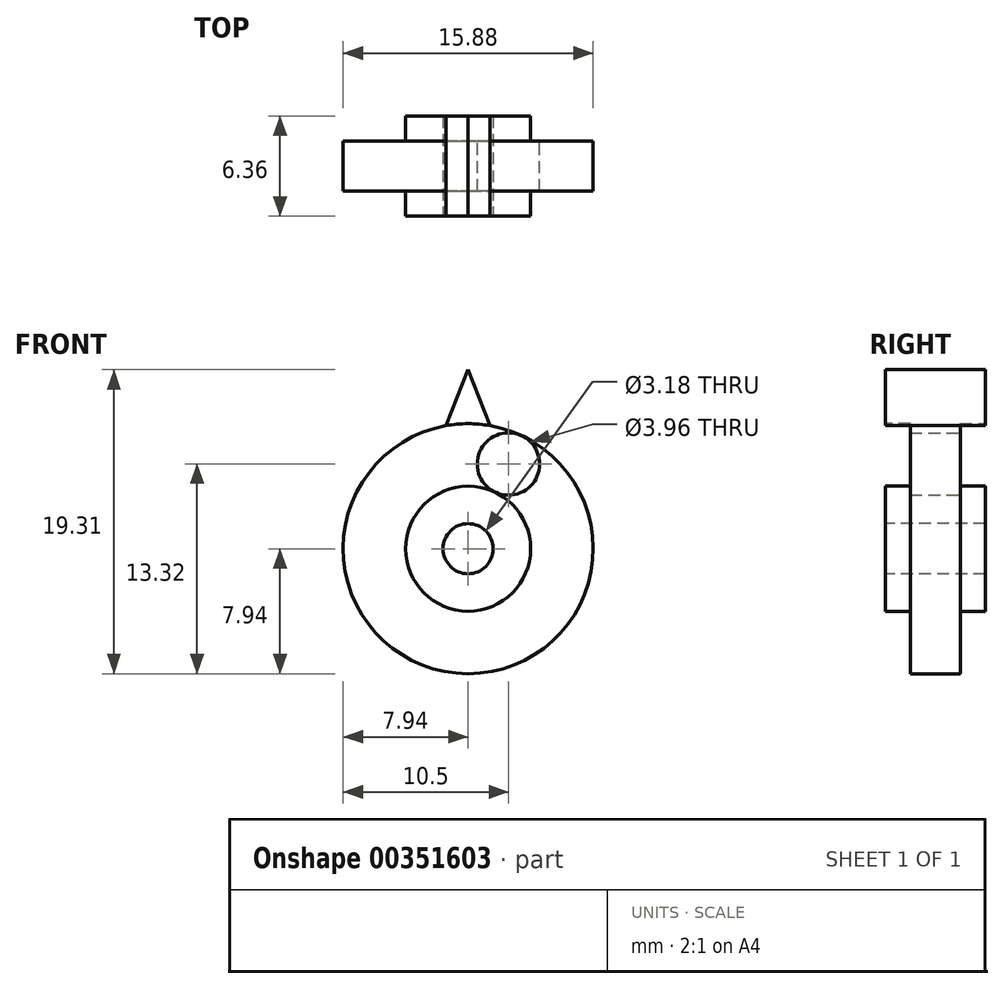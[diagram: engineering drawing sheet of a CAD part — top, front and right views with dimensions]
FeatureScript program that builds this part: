
annotation { "Feature Type Name" : "Feature", "Feature Type Description" : "" }
export const myFeature = defineFeature(function(context is Context, id is Id, definition is map)
    precondition{}
    {
        {
            var Q0;
            Q0=qCreatedBy(makeId("Front.planeOp"),FACE);
            var sketch = newSketch(context, id + "F0", { "sketchPlane" : qUnion([Q0])});
            skCircle(sketch, "E0", {"center": v(0, 0) * mm, "radius": 7.94 * mm});
            skSolve(sketch);
        }
        {
            var Q0;
            Q0 = qSketchRegion(id + "F0", true);
            extrude(context, id + "F1", {"entities" : qUnion([Q0]), "depth" : 6.35 * mm, "symmetric" : true});
        }
        {
            var Q0;
            Q0=makeQuery(id+"F1.opExtrude","CAP_FACE",FACE,{"disambiguationData":[OSD([sQuery(id+"F0.wireOp",EDGE,"E0")])],"isStart":false});
            var sketch = newSketch(context, id + "F2", { "sketchPlane" : qUnion([Q0])});
            skLineSegment(sketch, "E1", {"start": v(0, 11.37) * mm, "end": v(-1.4, 7.81) * mm});
            skLineSegment(sketch, "E2", {"start": v(0, 11.37) * mm, "end": v(1.4, 7.81) * mm});
            skArc(sketch, "E3.0", {"start": v(1.4, 7.81) * mm, "mid": v(0, 7.94) * mm, "end": v(-1.4, 7.81) * mm});
            skSolve(sketch);
        }
        {
            var Q0;
            Q0 = qSketchRegion(id + "F2", true);
            var Q1;
            Q1=makeQuery(id+"F1.opExtrude","CAP_FACE",FACE,{"disambiguationData":[OSD([sQuery(id+"F0.wireOp",EDGE,"E0")])],"isStart":true});
            extrude(context, id + "F3", {"entities" : qUnion([Q0]), "operationType" : NewBodyOperationType.ADD, "endBound" : BoundingType.UP_TO_SURFACE, "oppositeDirection" : true, "endBoundEntityFace" : qUnion([Q1]), "depth" : 25.4 * mm});
        }
        {
            var Q0;
            {var subQ0=sQuery(id+"F2.wireOp",EDGE,"E3.0");var subQ1=sQuery(id+"F2.wireOp",EDGE,"E2");var subQ2=sQuery(id+"F2.wireOp",EDGE,"E1");Q0=makeQuery(id+"FgbJZZofuTsAC2a_1.19.F3.boolean.opBoolean","MERGE",FACE,{"derivedFrom":[makeQuery(id+"FgbJZZofuTsAC2a_1.18.F3.boolean.opBoolean","MERGE",FACE,{"derivedFrom":[makeQuery(id+"FgbJZZofuTsAC2a_1.17.F3.boolean.opBoolean","MERGE",FACE,{"derivedFrom":[makeQuery(id+"FgbJZZofuTsAC2a_1.16.F3.boolean.opBoolean","MERGE",FACE,{"derivedFrom":[makeQuery(id+"FgbJZZofuTsAC2a_1.15.F3.boolean.opBoolean","MERGE",FACE,{"derivedFrom":[makeQuery(id+"FgbJZZofuTsAC2a_1.14.F3.boolean.opBoolean","MERGE",FACE,{"derivedFrom":[makeQuery(id+"FgbJZZofuTsAC2a_1.13.F3.boolean.opBoolean","MERGE",FACE,{"derivedFrom":[makeQuery(id+"FgbJZZofuTsAC2a_1.12.F3.boolean.opBoolean","MERGE",FACE,{"derivedFrom":[makeQuery(id+"FgbJZZofuTsAC2a_1.11.F3.boolean.opBoolean","MERGE",FACE,{"derivedFrom":[makeQuery(id+"FgbJZZofuTsAC2a_1.10.F3.boolean.opBoolean","MERGE",FACE,{"derivedFrom":[makeQuery(id+"FgbJZZofuTsAC2a_1.9.F3.boolean.opBoolean","MERGE",FACE,{"derivedFrom":[makeQuery(id+"FgbJZZofuTsAC2a_1.8.F3.boolean.opBoolean","MERGE",FACE,{"derivedFrom":[makeQuery(id+"FgbJZZofuTsAC2a_1.7.F3.boolean.opBoolean","MERGE",FACE,{"derivedFrom":[makeQuery(id+"FgbJZZofuTsAC2a_1.6.F3.boolean.opBoolean","MERGE",FACE,{"derivedFrom":[makeQuery(id+"FgbJZZofuTsAC2a_1.5.F3.boolean.opBoolean","MERGE",FACE,{"derivedFrom":[makeQuery(id+"FgbJZZofuTsAC2a_1.4.F3.boolean.opBoolean","MERGE",FACE,{"derivedFrom":[makeQuery(id+"FgbJZZofuTsAC2a_1.3.F3.boolean.opBoolean","MERGE",FACE,{"derivedFrom":[makeQuery(id+"FgbJZZofuTsAC2a_1.2.F3.boolean.opBoolean","MERGE",FACE,{"derivedFrom":[makeQuery(id+"FgbJZZofuTsAC2a_1.1.F3.boolean.opBoolean","MERGE",FACE,{"derivedFrom":[makeQuery(id+"F3.boolean.opBoolean","MERGE",FACE,{"derivedFrom":[makeQuery(id+"F1.opExtrude","CAP_FACE",FACE,{"disambiguationData":[OSD([sQuery(id+"F0.wireOp",EDGE,"E0")])],"isStart":false}),makeQuery(id+"F3.opExtrude","CAP_FACE",FACE,{"disambiguationData":[OSD([subQ2,subQ1,subQ0])],"isStart":true})]}),makeQuery(id+"FgbJZZofuTsAC2a_1.1.F3.opExtrude","CAP_FACE",FACE,{"disambiguationData":[OSD([subQ2,subQ1,subQ0])],"isStart":true})]}),makeQuery(id+"FgbJZZofuTsAC2a_1.2.F3.opExtrude","CAP_FACE",FACE,{"disambiguationData":[OSD([subQ2,subQ1,subQ0])],"isStart":true})]}),makeQuery(id+"FgbJZZofuTsAC2a_1.3.F3.opExtrude","CAP_FACE",FACE,{"disambiguationData":[OSD([subQ2,subQ1,subQ0])],"isStart":true})]}),makeQuery(id+"FgbJZZofuTsAC2a_1.4.F3.opExtrude","CAP_FACE",FACE,{"disambiguationData":[OSD([subQ2,subQ1,subQ0])],"isStart":true})]}),makeQuery(id+"FgbJZZofuTsAC2a_1.5.F3.opExtrude","CAP_FACE",FACE,{"disambiguationData":[OSD([subQ2,subQ1,subQ0])],"isStart":true})]}),makeQuery(id+"FgbJZZofuTsAC2a_1.6.F3.opExtrude","CAP_FACE",FACE,{"disambiguationData":[OSD([subQ2,subQ1,subQ0])],"isStart":true})]}),makeQuery(id+"FgbJZZofuTsAC2a_1.7.F3.opExtrude","CAP_FACE",FACE,{"disambiguationData":[OSD([subQ2,subQ1,subQ0])],"isStart":true})]}),makeQuery(id+"FgbJZZofuTsAC2a_1.8.F3.opExtrude","CAP_FACE",FACE,{"disambiguationData":[OSD([subQ2,subQ1,subQ0])],"isStart":true})]}),makeQuery(id+"FgbJZZofuTsAC2a_1.9.F3.opExtrude","CAP_FACE",FACE,{"disambiguationData":[OSD([subQ2,subQ1,subQ0])],"isStart":true})]}),makeQuery(id+"FgbJZZofuTsAC2a_1.10.F3.opExtrude","CAP_FACE",FACE,{"disambiguationData":[OSD([subQ2,subQ1,subQ0])],"isStart":true})]}),makeQuery(id+"FgbJZZofuTsAC2a_1.11.F3.opExtrude","CAP_FACE",FACE,{"disambiguationData":[OSD([subQ2,subQ1,subQ0])],"isStart":true})]}),makeQuery(id+"FgbJZZofuTsAC2a_1.12.F3.opExtrude","CAP_FACE",FACE,{"disambiguationData":[OSD([subQ2,subQ1,subQ0])],"isStart":true})]}),makeQuery(id+"FgbJZZofuTsAC2a_1.13.F3.opExtrude","CAP_FACE",FACE,{"disambiguationData":[OSD([subQ2,subQ1,subQ0])],"isStart":true})]}),makeQuery(id+"FgbJZZofuTsAC2a_1.14.F3.opExtrude","CAP_FACE",FACE,{"disambiguationData":[OSD([subQ2,subQ1,subQ0])],"isStart":true})]}),makeQuery(id+"FgbJZZofuTsAC2a_1.15.F3.opExtrude","CAP_FACE",FACE,{"disambiguationData":[OSD([subQ2,subQ1,subQ0])],"isStart":true})]}),makeQuery(id+"FgbJZZofuTsAC2a_1.16.F3.opExtrude","CAP_FACE",FACE,{"disambiguationData":[OSD([subQ2,subQ1,subQ0])],"isStart":true})]}),makeQuery(id+"FgbJZZofuTsAC2a_1.17.F3.opExtrude","CAP_FACE",FACE,{"disambiguationData":[OSD([subQ2,subQ1,subQ0])],"isStart":true})]}),makeQuery(id+"FgbJZZofuTsAC2a_1.18.F3.opExtrude","CAP_FACE",FACE,{"disambiguationData":[OSD([subQ2,subQ1,subQ0])],"isStart":true})]}),makeQuery(id+"FgbJZZofuTsAC2a_1.19.F3.opExtrude","CAP_FACE",FACE,{"disambiguationData":[OSD([subQ2,subQ1,subQ0])],"isStart":true})]});}
            var sketch = newSketch(context, id + "F4", { "sketchPlane" : qUnion([Q0])});
            skCircle(sketch, "E4", {"center": v(0, 0) * mm, "radius": 7.94 * mm});
            skSolve(sketch);
        }
        {
            var Q0;
            Q0 = qSketchRegion(id + "F4", true);
            extrude(context, id + "F5", {"entities" : qUnion([Q0]), "operationType" : NewBodyOperationType.REMOVE, "oppositeDirection" : true, "depth" : 1.59 * mm});
        }
        {
            var Q0;
            Q0=makeQuery(id+"F5.boolean.opBoolean","COPY",FACE,{"derivedFrom":makeQuery(id+"F5.opExtrude","CAP_FACE",FACE,{"disambiguationData":[OSD([sQuery(id+"F4.wireOp",EDGE,"E4")])],"isStart":false})});
            var sketch = newSketch(context, id + "F6", { "sketchPlane" : qUnion([Q0])});
            skCircle(sketch, "E5", {"center": v(0, 0) * mm, "radius": 3.97 * mm});
            skSolve(sketch);
        }
        {
            var Q0;
            Q0 = qSketchRegion(id + "F6", true);
            extrude(context, id + "F7", {"entities" : qUnion([Q0]), "operationType" : NewBodyOperationType.ADD, "depth" : 1.59 * mm});
        }
        {
            var Q0;
            Q0=makeQuery(id+"F7.opExtrude","CAP_FACE",FACE,{"disambiguationData":[OSD([sQuery(id+"F6.wireOp",EDGE,"E5")])],"isStart":false});
            var sketch = newSketch(context, id + "F8", { "sketchPlane" : qUnion([Q0])});
            skCircle(sketch, "E6", {"center": v(0, 0) * mm, "radius": 1.59 * mm});
            skSolve(sketch);
        }
        {
            var Q0;
            Q0 = qSketchRegion(id + "F8", true);
            extrude(context, id + "F9", {"entities" : qUnion([Q0]), "operationType" : NewBodyOperationType.REMOVE, "endBound" : BoundingType.THROUGH_ALL, "oppositeDirection" : true, "depth" : 25.4 * mm});
        }
        {
            var Q0;
            {var subQ0=sQuery(id+"F0.wireOp",EDGE,"E0");Q0=makeQuery(id+"FgbJZZofuTsAC2a_1.19.F3.boolean.opBoolean","MERGE",FACE,{"derivedFrom":[makeQuery(id+"FgbJZZofuTsAC2a_1.18.F3.boolean.opBoolean","MERGE",FACE,{"derivedFrom":[makeQuery(id+"FgbJZZofuTsAC2a_1.17.F3.boolean.opBoolean","MERGE",FACE,{"derivedFrom":[makeQuery(id+"FgbJZZofuTsAC2a_1.16.F3.boolean.opBoolean","MERGE",FACE,{"derivedFrom":[makeQuery(id+"FgbJZZofuTsAC2a_1.15.F3.boolean.opBoolean","MERGE",FACE,{"derivedFrom":[makeQuery(id+"FgbJZZofuTsAC2a_1.14.F3.boolean.opBoolean","MERGE",FACE,{"derivedFrom":[makeQuery(id+"FgbJZZofuTsAC2a_1.13.F3.boolean.opBoolean","MERGE",FACE,{"derivedFrom":[makeQuery(id+"FgbJZZofuTsAC2a_1.12.F3.boolean.opBoolean","MERGE",FACE,{"derivedFrom":[makeQuery(id+"FgbJZZofuTsAC2a_1.11.F3.boolean.opBoolean","MERGE",FACE,{"derivedFrom":[makeQuery(id+"FgbJZZofuTsAC2a_1.10.F3.boolean.opBoolean","MERGE",FACE,{"derivedFrom":[makeQuery(id+"FgbJZZofuTsAC2a_1.9.F3.boolean.opBoolean","MERGE",FACE,{"derivedFrom":[makeQuery(id+"FgbJZZofuTsAC2a_1.8.F3.boolean.opBoolean","MERGE",FACE,{"derivedFrom":[makeQuery(id+"FgbJZZofuTsAC2a_1.7.F3.boolean.opBoolean","MERGE",FACE,{"derivedFrom":[makeQuery(id+"FgbJZZofuTsAC2a_1.6.F3.boolean.opBoolean","MERGE",FACE,{"derivedFrom":[makeQuery(id+"FgbJZZofuTsAC2a_1.5.F3.boolean.opBoolean","MERGE",FACE,{"derivedFrom":[makeQuery(id+"FgbJZZofuTsAC2a_1.4.F3.boolean.opBoolean","MERGE",FACE,{"derivedFrom":[makeQuery(id+"FgbJZZofuTsAC2a_1.3.F3.boolean.opBoolean","MERGE",FACE,{"derivedFrom":[makeQuery(id+"FgbJZZofuTsAC2a_1.2.F3.boolean.opBoolean","MERGE",FACE,{"derivedFrom":[makeQuery(id+"FgbJZZofuTsAC2a_1.1.F3.boolean.opBoolean","MERGE",FACE,{"derivedFrom":[makeQuery(id+"F3.boolean.opBoolean","MERGE",FACE,{"derivedFrom":[makeQuery(id+"F1.opExtrude","CAP_FACE",FACE,{"disambiguationData":[OSD([subQ0])],"isStart":true}),makeQuery(id+"F3.opExtrude","CAP_FACE",FACE,{"disambiguationData":[OSD([subQ0])],"isStart":false})]}),makeQuery(id+"FgbJZZofuTsAC2a_1.1.F3.opExtrude","CAP_FACE",FACE,{"disambiguationData":[OSD([subQ0])],"isStart":false})]}),makeQuery(id+"FgbJZZofuTsAC2a_1.2.F3.opExtrude","CAP_FACE",FACE,{"disambiguationData":[OSD([subQ0])],"isStart":false})]}),makeQuery(id+"FgbJZZofuTsAC2a_1.3.F3.opExtrude","CAP_FACE",FACE,{"disambiguationData":[OSD([subQ0])],"isStart":false})]}),makeQuery(id+"FgbJZZofuTsAC2a_1.4.F3.opExtrude","CAP_FACE",FACE,{"disambiguationData":[OSD([subQ0])],"isStart":false})]}),makeQuery(id+"FgbJZZofuTsAC2a_1.5.F3.opExtrude","CAP_FACE",FACE,{"disambiguationData":[OSD([subQ0])],"isStart":false})]}),makeQuery(id+"FgbJZZofuTsAC2a_1.6.F3.opExtrude","CAP_FACE",FACE,{"disambiguationData":[OSD([subQ0])],"isStart":false})]}),makeQuery(id+"FgbJZZofuTsAC2a_1.7.F3.opExtrude","CAP_FACE",FACE,{"disambiguationData":[OSD([subQ0])],"isStart":false})]}),makeQuery(id+"FgbJZZofuTsAC2a_1.8.F3.opExtrude","CAP_FACE",FACE,{"disambiguationData":[OSD([subQ0])],"isStart":false})]}),makeQuery(id+"FgbJZZofuTsAC2a_1.9.F3.opExtrude","CAP_FACE",FACE,{"disambiguationData":[OSD([subQ0])],"isStart":false})]}),makeQuery(id+"FgbJZZofuTsAC2a_1.10.F3.opExtrude","CAP_FACE",FACE,{"disambiguationData":[OSD([subQ0])],"isStart":false})]}),makeQuery(id+"FgbJZZofuTsAC2a_1.11.F3.opExtrude","CAP_FACE",FACE,{"disambiguationData":[OSD([subQ0])],"isStart":false})]}),makeQuery(id+"FgbJZZofuTsAC2a_1.12.F3.opExtrude","CAP_FACE",FACE,{"disambiguationData":[OSD([subQ0])],"isStart":false})]}),makeQuery(id+"FgbJZZofuTsAC2a_1.13.F3.opExtrude","CAP_FACE",FACE,{"disambiguationData":[OSD([subQ0])],"isStart":false})]}),makeQuery(id+"FgbJZZofuTsAC2a_1.14.F3.opExtrude","CAP_FACE",FACE,{"disambiguationData":[OSD([subQ0])],"isStart":false})]}),makeQuery(id+"FgbJZZofuTsAC2a_1.15.F3.opExtrude","CAP_FACE",FACE,{"disambiguationData":[OSD([subQ0])],"isStart":false})]}),makeQuery(id+"FgbJZZofuTsAC2a_1.16.F3.opExtrude","CAP_FACE",FACE,{"disambiguationData":[OSD([subQ0])],"isStart":false})]}),makeQuery(id+"FgbJZZofuTsAC2a_1.17.F3.opExtrude","CAP_FACE",FACE,{"disambiguationData":[OSD([subQ0])],"isStart":false})]}),makeQuery(id+"FgbJZZofuTsAC2a_1.18.F3.opExtrude","CAP_FACE",FACE,{"disambiguationData":[OSD([subQ0])],"isStart":false})]}),makeQuery(id+"FgbJZZofuTsAC2a_1.19.F3.opExtrude","CAP_FACE",FACE,{"disambiguationData":[OSD([subQ0])],"isStart":false})]});}
            var sketch = newSketch(context, id + "F10", { "sketchPlane" : qUnion([Q0])});
            skCircle(sketch, "E7", {"center": v(0, 0) * mm, "radius": 7.94 * mm});
            skSolve(sketch);
        }
        {
            var Q0;
            Q0 = qSketchRegion(id + "F10", true);
            extrude(context, id + "F11", {"entities" : qUnion([Q0]), "operationType" : NewBodyOperationType.REMOVE, "oppositeDirection" : true, "depth" : 1.59 * mm});
        }
        {
            var Q0;
            Q0=makeQuery(id+"F11.boolean.opBoolean","COPY",FACE,{"derivedFrom":makeQuery(id+"F11.opExtrude","CAP_FACE",FACE,{"disambiguationData":[OSD([sQuery(id+"F10.wireOp",EDGE,"E7")])],"isStart":false})});
            var sketch = newSketch(context, id + "F12", { "sketchPlane" : qUnion([Q0])});
            skCircle(sketch, "E8", {"center": v(0, 0) * mm, "radius": 3.97 * mm});
            skSolve(sketch);
        }
        {
            var Q0;
            Q0 = qSketchRegion(id + "F12", true);
            extrude(context, id + "F13", {"entities" : qUnion([Q0]), "operationType" : NewBodyOperationType.ADD, "depth" : 1.59 * mm});
        }
        {
            var Q0;
            Q0=makeQuery(id+"F13.opExtrude","CAP_FACE",FACE,{"disambiguationData":[OSD([sQuery(id+"F12.wireOp",EDGE,"E8")])],"isStart":false});
            var sketch = newSketch(context, id + "F14", { "sketchPlane" : qUnion([Q0])});
            skCircle(sketch, "E9", {"center": v(0, 0) * mm, "radius": 1.59 * mm});
            skSolve(sketch);
        }
        {
            var Q0;
            Q0 = qSketchRegion(id + "F14", true);
            extrude(context, id + "F15", {"entities" : qUnion([Q0]), "operationType" : NewBodyOperationType.REMOVE, "endBound" : BoundingType.THROUGH_ALL, "oppositeDirection" : true, "depth" : 25.4 * mm});
        }
        {
            var Q0;
            Q0=makeQuery(id+"F11.boolean.opBoolean","COPY",FACE,{"derivedFrom":makeQuery(id+"F11.opExtrude","CAP_FACE",FACE,{"disambiguationData":[OSD([sQuery(id+"F10.wireOp",EDGE,"E7")])],"isStart":false})});
            var sketch = newSketch(context, id + "F16", { "sketchPlane" : qUnion([Q0])});
            skCircle(sketch, "E10", {"center": v(-2.56, 5.38) * mm, "radius": 1.98 * mm});
            skSolve(sketch);
        }
        {
            var Q0;
            Q0 = qSketchRegion(id + "F16", true);
            extrude(context, id + "F17", {"entities" : qUnion([Q0]), "operationType" : NewBodyOperationType.REMOVE, "endBound" : BoundingType.THROUGH_ALL, "oppositeDirection" : true, "depth" : 25.4 * mm});
        }
    });
